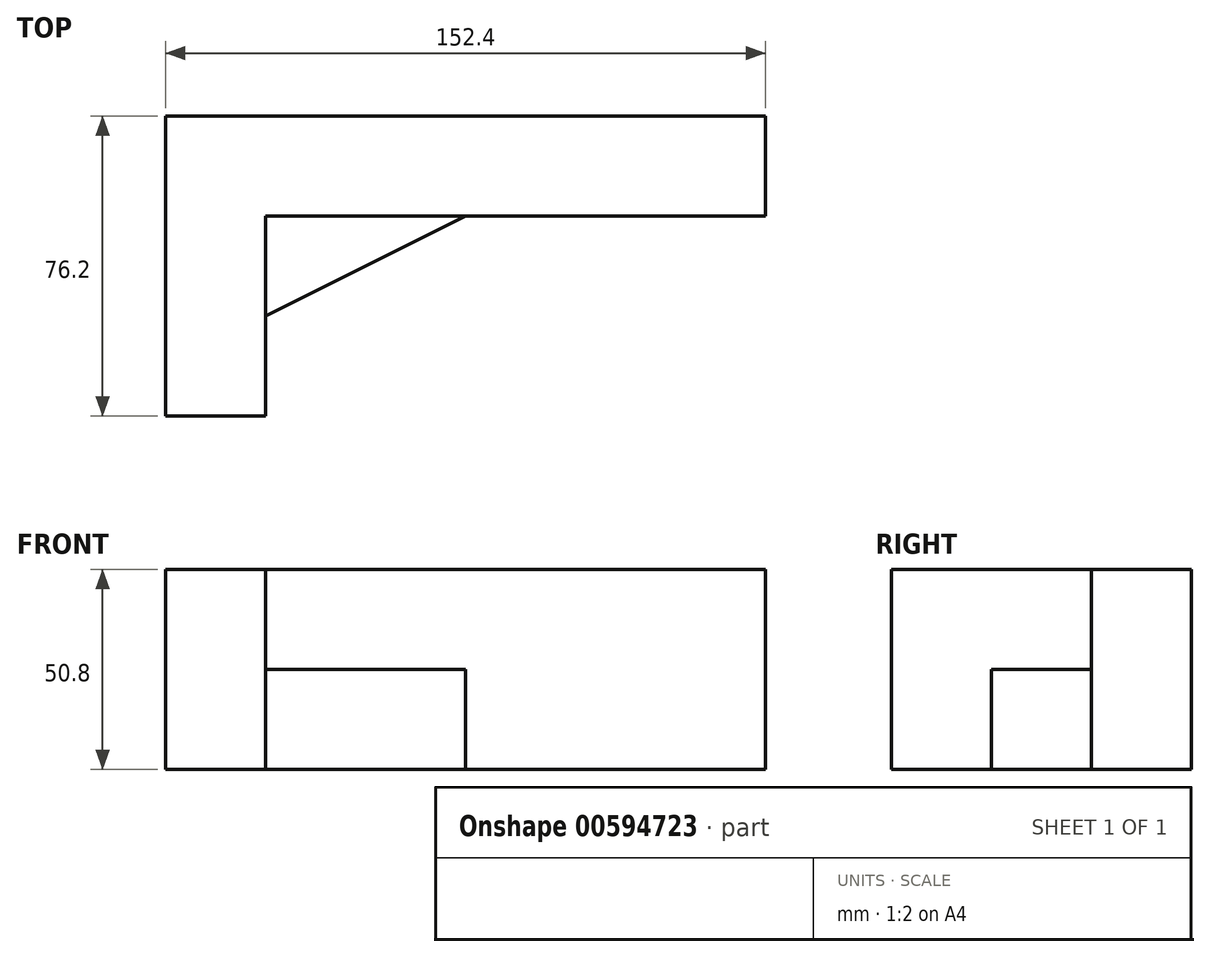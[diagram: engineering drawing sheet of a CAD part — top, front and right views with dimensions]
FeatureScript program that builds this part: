
annotation { "Feature Type Name" : "Feature", "Feature Type Description" : "" }
export const myFeature = defineFeature(function(context is Context, id is Id, definition is map)
    precondition{}
    {
        {
            var Q0;
            Q0=qCreatedBy(makeId("Front.planeOp"),FACE);
            var sketch = newSketch(context, id + "F0", { "sketchPlane" : qUnion([Q0])});
            skLineSegment(sketch, "E0.bottom", {"start": v(0, 0) * mm, "end": v(152.4, 0) * mm});
            skLineSegment(sketch, "E0.top", {"start": v(0, 50.8) * mm, "end": v(152.4, 50.8) * mm});
            skLineSegment(sketch, "E0.left", {"start": v(0, 0) * mm, "end": v(0, 50.8) * mm});
            skLineSegment(sketch, "E0.right", {"start": v(152.4, 0) * mm, "end": v(152.4, 50.8) * mm});
            skLineSegment(sketch, "E1", {"start": v(0, 0) * mm, "end": v(25.4, 0) * mm});
            skLineSegment(sketch, "E2", {"start": v(25.4, 0) * mm, "end": v(25.4, 50.8) * mm});
            skLineSegment(sketch, "E3", {"start": v(0, 50.8) * mm, "end": v(25.4, 50.8) * mm});
            skSolve(sketch);
        }
        {
            var Q0;
            Q0 = qSketchRegion(id + "F0", true);
            extrude(context, id + "F1", {"entities" : qUnion([Q0]), "depth" : 76.2 * mm, "offsetDistance" : 25.4 * mm});
        }
        {
            var Q0;
            Q0=makeQuery(id+"F1.opExtrude","CAP_FACE",FACE,{"disambiguationData":[OSD([sQuery(id+"F0.wireOp",EDGE,"E0.bottom"),sQuery(id+"F0.wireOp",EDGE,"E0.top"),sQuery(id+"F0.wireOp",EDGE,"E0.left"),sQuery(id+"F0.wireOp",EDGE,"E0.right"),sQuery(id+"F0.wireOp",EDGE,"E1"),sQuery(id+"F0.wireOp",EDGE,"E3")])],"isStart":false});
            var sketch = newSketch(context, id + "F2", { "sketchPlane" : qUnion([Q0])});
            skLineSegment(sketch, "E4", {"start": v(0, 0) * mm, "end": v(25.4, 0) * mm});
            skLineSegment(sketch, "E5", {"start": v(25.4, 0) * mm, "end": v(25.4, 50.8) * mm});
            skLineSegment(sketch, "E6", {"start": v(25.4, 50.8) * mm, "end": v(0, 50.8) * mm});
            skLineSegment(sketch, "E7", {"start": v(0, 50.8) * mm, "end": v(0, 0) * mm});
            skLineSegment(sketch, "E8", {"start": v(25.4, 50.8) * mm, "end": v(152.4, 50.8) * mm});
            skLineSegment(sketch, "E9", {"start": v(152.4, 50.8) * mm, "end": v(152.4, 0) * mm});
            skLineSegment(sketch, "E10", {"start": v(152.4, 0) * mm, "end": v(25.4, 0) * mm});
            skSolve(sketch);
        }
        {
            var Q0;
            Q0=makeQuery(id+"F2.imprint","IMPRINT",FACE,{"disambiguationData":[TD([[makeQuery(id+"F2.imprint","IMPRINT",EDGE,{"derivedFrom":sQuery(id+"F2.wireOp",EDGE,"E5")}),-1.0]])]});
            extrude(context, id + "F3", {"entities" : qUnion([Q0]), "operationType" : NewBodyOperationType.REMOVE, "oppositeDirection" : true, "depth" : 50.8 * mm, "offsetDistance" : 25.4 * mm});
        }
        {
            var Q0;
            Q0=makeQuery(id+"F1.opExtrude","SWEPT_FACE",FACE,{"disambiguationData":[OSD([sQuery(id+"F0.wireOp",EDGE,"E0.bottom"),sQuery(id+"F0.wireOp",EDGE,"E1")])]});
            var sketch = newSketch(context, id + "F4", { "sketchPlane" : qUnion([Q0])});
            skLineSegment(sketch, "E11", {"start": v(25.4, 76.2) * mm, "end": v(25.4, 50.8) * mm});
            skLineSegment(sketch, "E12", {"start": v(25.4, 50.8) * mm, "end": v(25.4, 25.4) * mm});
            skLineSegment(sketch, "E13", {"start": v(25.4, 25.4) * mm, "end": v(76.2, 25.4) * mm});
            skLineSegment(sketch, "E14", {"start": v(76.2, 25.4) * mm, "end": v(25.4, 50.8) * mm});
            skSolve(sketch);
        }
        {
            var Q0;
            Q0 = qSketchRegion(id + "F4", true);
            extrude(context, id + "F5", {"entities" : qUnion([Q0]), "oppositeDirection" : true, "depth" : 25.4 * mm, "offsetDistance" : 25.4 * mm});
        }
    });
